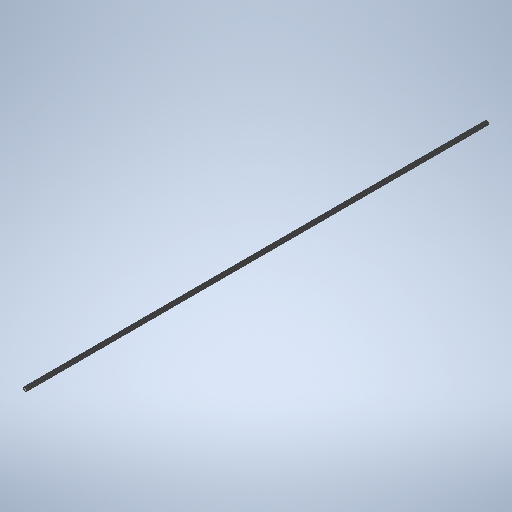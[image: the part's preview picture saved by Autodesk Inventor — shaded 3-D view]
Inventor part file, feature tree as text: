
AUTODESK INVENTOR PART (.ipt)
format: ipt  version: 2025.2 (Build 292293000, 293)  size: 3,622,400 bytes
history: native  units: mm
features: extrude x1, chamfer x1, other x1, pattern_circular x1
ambient origin geometry x8: Origin, YZ Plane, XZ Plane, XY Plane, X Axis, Y Axis, Z Axis, Center Point
bodies: Solid1 (feature_tree)
feature tree (4):
  extrude  "1000mm Rod"  Depth=1000.0mm TaperAngle=0.0deg
  chamfer  "Chamfer1"  Distance=0.907143mm Angle=45.0deg
  other  "ACME Thread 2mm Pitch"
  pattern_circular  "4 Start"  [2 undecoded]
note: 2 required parameter values undecoded (feature->parameter linkage not recoverable at this tier; creation-order binding heuristic only, values carry confidence <= 0.55)
